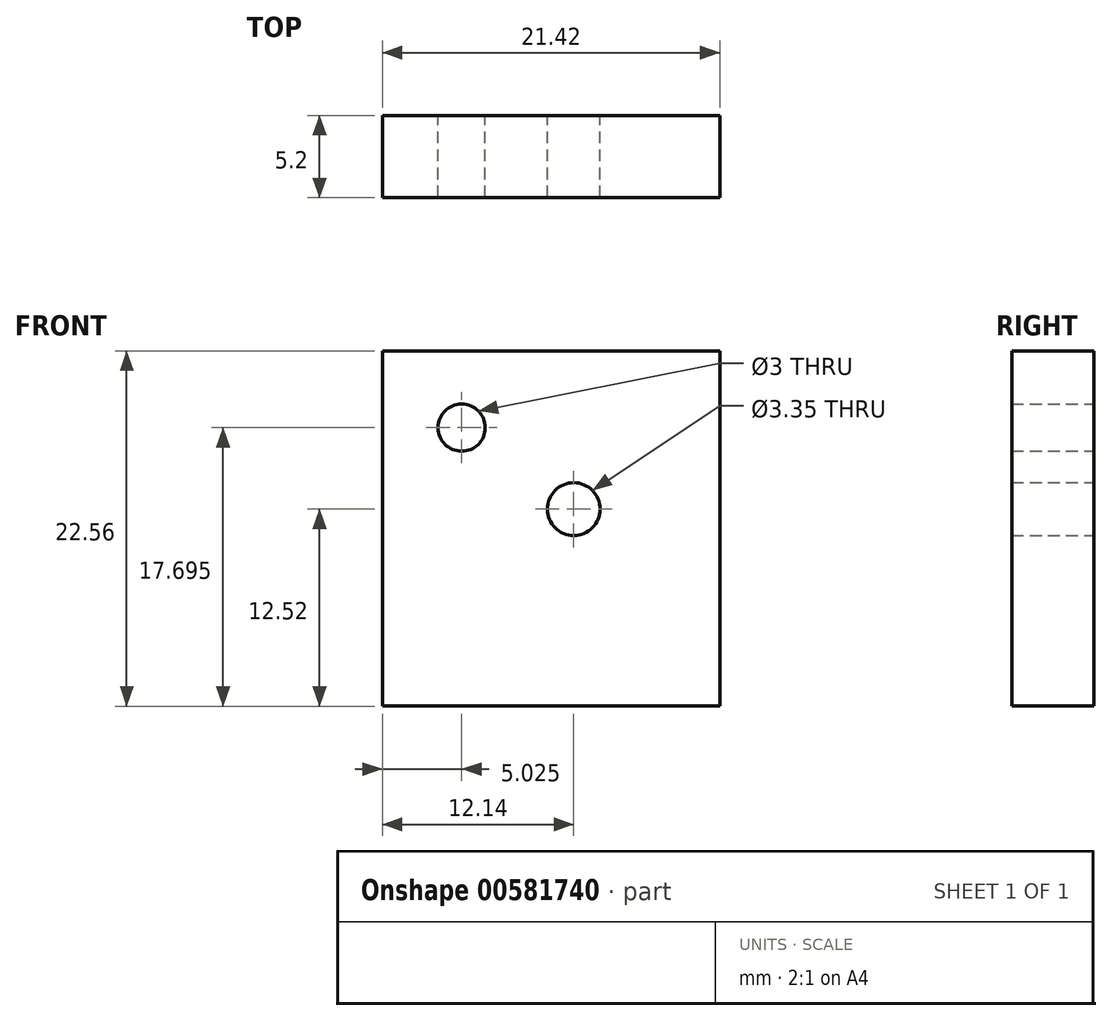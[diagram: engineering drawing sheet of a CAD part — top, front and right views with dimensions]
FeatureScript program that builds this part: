
annotation { "Feature Type Name" : "Feature", "Feature Type Description" : "" }
export const myFeature = defineFeature(function(context is Context, id is Id, definition is map)
    precondition{}
    {
        {
            var Q0;
            Q0=qCreatedBy(makeId("Front.planeOp"),FACE);
            var sketch = newSketch(context, id + "F0", { "sketchPlane" : qUnion([Q0])});
            skLineSegment(sketch, "E0.bottom", {"start": v(-10.71, 11.28) * mm, "end": v(10.72, 11.28) * mm});
            skLineSegment(sketch, "E0.top", {"start": v(-10.72, -11.28) * mm, "end": v(10.71, -11.28) * mm});
            skLineSegment(sketch, "E0.left", {"start": v(-10.71, 11.28) * mm, "end": v(-10.72, -11.28) * mm});
            skLineSegment(sketch, "E0.right", {"start": v(10.72, 11.28) * mm, "end": v(10.71, -11.28) * mm});
            skPoint(sketch, "E0.middle", {"position": v(0, 0) * mm});
            skCircle(sketch, "E1", {"center": v(-5.68, 6.41) * mm, "radius": 1.5 * mm});
            skCircle(sketch, "E2", {"center": v(1.43, 1.24) * mm, "radius": 1.68 * mm});
            skSolve(sketch);
        }
        {
            var Q0;
            Q0=makeQuery(id+"F0.imprint","IMPRINT",FACE,{"disambiguationData":[TD([[makeQuery(id+"F0.imprint","IMPRINT",EDGE,{"derivedFrom":sQuery(id+"F0.wireOp",EDGE,"E0.bottom")}),-1.0]])]});
            extrude(context, id + "F1", {"entities" : qUnion([Q0]), "depth" : 5.2 * mm, "offsetDistance" : 25 * mm});
        }
    });
